annotation { "Feature Type Name" : "Feature", "Feature Type Description" : "" }
export const myFeature = defineFeature(function(context is Context, id is Id, definition is map)
    precondition{}
    {
        {
            var Q0;
            Q0=qCreatedBy(makeId("Front.planeOp"),FACE);
            var sketch = newSketch(context, id + "F0", { "sketchPlane" : qUnion([Q0])});
            skCircle(sketch, "E0", {"center": v(0, 0) * mm, "radius": 11 * mm});
            skCircle(sketch, "E1", {"center": v(0, 0) * mm, "radius": 14.29 * mm});
            skCircle(sketch, "E2", {"center": v(0, 31.75) * mm, "radius": 11 * mm});
            skCircle(sketch, "E3", {"center": v(0, 31.75) * mm, "radius": 14.29 * mm});
            skCircle(sketch, "E4.1.0", {"center": v(-27.5, -15.87) * mm, "radius": 14.29 * mm});
            skCircle(sketch, "E4.1.1", {"center": v(-27.5, -15.87) * mm, "radius": 11 * mm});
            skCircle(sketch, "E4.2.0", {"center": v(27.5, -15.88) * mm, "radius": 14.29 * mm});
            skCircle(sketch, "E4.2.1", {"center": v(27.5, -15.88) * mm, "radius": 11 * mm});
            skSolve(sketch);
        }
        {
            var Q0;
            Q0=qCreatedBy(makeId("Front.planeOp"),FACE);
            var sketch = newSketch(context, id + "F1", { "sketchPlane" : qUnion([Q0])});
            skCircle(sketch, "E5.0", {"center": v(0, 31.75) * mm, "radius": 11 * mm});
            skCircle(sketch, "E6.0", {"center": v(0, 31.75) * mm, "radius": 14.29 * mm});
            skCircle(sketch, "E7.0", {"center": v(0, 0) * mm, "radius": 14.29 * mm});
            skCircle(sketch, "E8.0", {"center": v(0, 0) * mm, "radius": 11 * mm});
            skCircle(sketch, "E9.0", {"center": v(-27.5, -15.87) * mm, "radius": 14.29 * mm});
            skCircle(sketch, "E10.0", {"center": v(-27.5, -15.87) * mm, "radius": 11 * mm});
            skCircle(sketch, "E11.0", {"center": v(27.5, -15.88) * mm, "radius": 14.29 * mm});
            skCircle(sketch, "E12.0", {"center": v(27.5, -15.88) * mm, "radius": 11 * mm});
            skCircle(sketch, "E13", {"center": v(0, 0) * mm, "radius": 31.75 * mm});
            skCircle(sketch, "E14", {"center": v(0, 0) * mm, "radius": 28.58 * mm});
            skPoint(sketch, "E15", {"position": v(-28.53, -1.62) * mm});
            skPoint(sketch, "E16", {"position": v(-12.86, 25.52) * mm});
            skArc(sketch, "E17", {"start": v(-28.53, -1.62) * mm, "mid": v(-19, 10.96) * mm, "end": v(-12.86, 25.52) * mm});
            skArc(sketch, "E18.1.0", {"start": v(15.67, -23.9) * mm, "mid": v(0, -21.93) * mm, "end": v(-15.67, -23.9) * mm});
            skArc(sketch, "E18.2.0", {"start": v(12.86, 25.52) * mm, "mid": v(19, 10.96) * mm, "end": v(28.53, -1.62) * mm});
            skPoint(sketch, "E19", {"position": v(12.86, 25.52) * mm});
            skPoint(sketch, "E20", {"position": v(28.53, -1.62) * mm});
            skPoint(sketch, "E21", {"position": v(15.67, -23.9) * mm});
            skPoint(sketch, "E22", {"position": v(-15.67, -23.9) * mm});
            skPoint(sketch, "E23", {"position": v(-39.01, -51.78) * mm});
            skSolve(sketch);
        }
        {
            var Q0;
            Q0=qCreatedBy(makeId("Front.planeOp"),FACE);
            var sketch = newSketch(context, id + "F2", { "sketchPlane" : qUnion([Q0])});
            skCircle(sketch, "E24.0.0", {"center": v(0, 31.75) * mm, "radius": 11 * mm});
            skArc(sketch, "E25.0", {"start": v(-12.86, 25.52) * mm, "mid": v(-8.37, 20.17) * mm, "end": v(-1.88, 17.59) * mm});
            skArc(sketch, "E26.0", {"start": v(-15.34, 27.8) * mm, "mid": v(-27.5, 15.87) * mm, "end": v(-31.74, -0.61) * mm});
            skArc(sketch, "E27.0", {"start": v(-16.71, 23.18) * mm, "mid": v(-24.75, 14.29) * mm, "end": v(-28.43, 2.89) * mm});
            skArc(sketch, "E28.0", {"start": v(-28.53, -1.62) * mm, "mid": v(-19, 10.96) * mm, "end": v(-12.86, 25.52) * mm});
            skArc(sketch, "E29.0", {"start": v(12.86, 25.52) * mm, "mid": v(19, 10.96) * mm, "end": v(28.53, -1.62) * mm});
            skArc(sketch, "E30.0", {"start": v(-1.88, 14.16) * mm, "mid": v(-12.39, 7.12) * mm, "end": v(-13.18, -5.51) * mm});
            skArc(sketch, "E31.0.0", {"start": v(15.67, -23.9) * mm, "mid": v(13.28, -17.3) * mm, "end": v(14.31, -10.36) * mm});
            skArc(sketch, "E31.0.1", {"start": v(28.53, -1.62) * mm, "mid": v(19, 10.96) * mm, "end": v(12.86, 25.52) * mm});
            skArc(sketch, "E31.0.2", {"start": v(12.86, 25.52) * mm, "mid": v(8.34, 20.15) * mm, "end": v(1.82, 17.58) * mm});
            skArc(sketch, "E31.0.3", {"start": v(-12.86, 25.52) * mm, "mid": v(-19, 10.96) * mm, "end": v(-28.53, -1.62) * mm});
            skArc(sketch, "E31.0.4", {"start": v(-28.53, -1.62) * mm, "mid": v(-21.62, -2.85) * mm, "end": v(-16.13, -7.21) * mm});
            skArc(sketch, "E31.0.5", {"start": v(-15.67, -23.9) * mm, "mid": v(0, -21.93) * mm, "end": v(15.67, -23.9) * mm});
            skArc(sketch, "E32.0", {"start": v(21.89, -29.02) * mm, "mid": v(39.87, -23.02) * mm, "end": v(36.07, -4.45) * mm});
            skArc(sketch, "E33.0.0", {"start": v(-11.71, -26.06) * mm, "mid": v(0, -28.58) * mm, "end": v(11.71, -26.06) * mm});
            skArc(sketch, "E33.0.1", {"start": v(15.67, -23.9) * mm, "mid": v(0, -21.93) * mm, "end": v(-15.67, -23.9) * mm});
            skArc(sketch, "E34.0", {"start": v(-16.13, -7.21) * mm, "mid": v(-21.62, -2.85) * mm, "end": v(-28.53, -1.62) * mm});
            skArc(sketch, "E35.0.0", {"start": v(-36.07, -4.45) * mm, "mid": v(-39.87, -23.02) * mm, "end": v(-21.89, -29.02) * mm});
            skCircle(sketch, "E36.0", {"center": v(-27.5, -15.87) * mm, "radius": 11 * mm});
            skCircle(sketch, "E37.0", {"center": v(27.5, -15.88) * mm, "radius": 11 * mm});
            skCircle(sketch, "E38.0.0", {"center": v(0, 0) * mm, "radius": 11 * mm});
            skArc(sketch, "E39", {"start": v(-36.67, -4.93) * mm, "mid": v(-34.15, -2.84) * mm, "end": v(-31.74, -0.61) * mm});
            skArc(sketch, "E40.1.0", {"start": v(22.6, -29.3) * mm, "mid": v(19.53, -28.16) * mm, "end": v(16.4, -27.18) * mm});
            skArc(sketch, "E40.2.0", {"start": v(14.07, 34.22) * mm, "mid": v(14.62, 31) * mm, "end": v(15.34, 27.8) * mm});
            skPoint(sketch, "E41", {"position": v(-28.43, 2.89) * mm});
            skPoint(sketch, "E42", {"position": v(-16.71, 23.18) * mm});
            skPoint(sketch, "E43", {"position": v(16.71, 23.18) * mm});
            skPoint(sketch, "E44", {"position": v(28.43, 2.89) * mm});
            skPoint(sketch, "E45", {"position": v(-11.71, -26.06) * mm});
            skPoint(sketch, "E46", {"position": v(11.71, -26.06) * mm});
            skArc(sketch, "E47.trimOffspring", {"start": v(-15.34, 27.8) * mm, "mid": v(-14.62, 31) * mm, "end": v(-14.07, 34.22) * mm});
            skArc(sketch, "E48.trimOffspring", {"start": v(-28.43, 2.89) * mm, "mid": v(-21.58, 12.46) * mm, "end": v(-16.71, 23.18) * mm});
            skArc(sketch, "E49.trimOffspring", {"start": v(16.71, 23.18) * mm, "mid": v(21.58, 12.46) * mm, "end": v(28.43, 2.89) * mm});
            skArc(sketch, "E50.trimOffspring", {"start": v(31.74, -0.61) * mm, "mid": v(34.15, -2.84) * mm, "end": v(36.67, -4.93) * mm});
            skArc(sketch, "E51.trimOffspring", {"start": v(28.43, 2.89) * mm, "mid": v(24.75, 14.29) * mm, "end": v(16.71, 23.18) * mm});
            skArc(sketch, "E52.trimOffspring", {"start": v(31.74, -0.61) * mm, "mid": v(27.5, 15.87) * mm, "end": v(15.34, 27.8) * mm});
            skArc(sketch, "E53.trimOffspring", {"start": v(11.71, -26.06) * mm, "mid": v(0, -24.92) * mm, "end": v(-11.71, -26.06) * mm});
            skArc(sketch, "E54.trimOffspring", {"start": v(-16.4, -27.18) * mm, "mid": v(-19.53, -28.16) * mm, "end": v(-22.6, -29.3) * mm});
            skArc(sketch, "E55.trimOffspring", {"start": v(-16.4, -27.18) * mm, "mid": v(0, -31.75) * mm, "end": v(16.4, -27.18) * mm});
            skArc(sketch, "E56.trimOffspring", {"start": v(-11.71, -26.06) * mm, "mid": v(0, -28.57) * mm, "end": v(11.71, -26.06) * mm});
            skArc(sketch, "E57.trimOffspring", {"start": v(-15.67, -23.9) * mm, "mid": v(-13.28, -17.33) * mm, "end": v(-14.3, -10.42) * mm});
            skArc(sketch, "E58.trimOffspring", {"start": v(14.18, 33.46) * mm, "mid": v(0, 46.04) * mm, "end": v(-14.18, 33.46) * mm});
            skLineSegment(sketch, "E59", {"start": v(-1.88, 17.59) * mm, "end": v(-1.88, 14.16) * mm});
            skLineSegment(sketch, "E60", {"start": v(1.82, 17.58) * mm, "end": v(1.82, 14.17) * mm});
            skLineSegment(sketch, "E61.1.0", {"start": v(-16.13, -7.21) * mm, "end": v(-13.18, -5.51) * mm});
            skLineSegment(sketch, "E61.1.1", {"start": v(-14.3, -10.42) * mm, "end": v(-11.33, -8.71) * mm});
            skLineSegment(sketch, "E61.2.0", {"start": v(14.31, -10.36) * mm, "end": v(11.36, -8.66) * mm});
            skLineSegment(sketch, "E61.2.1", {"start": v(16.17, -7.16) * mm, "end": v(13.2, -5.45) * mm});
            skArc(sketch, "E62.trimOffspring", {"start": v(-14.3, -10.42) * mm, "mid": v(-13.28, -17.33) * mm, "end": v(-15.67, -23.9) * mm});
            skArc(sketch, "E63.trimOffspring", {"start": v(16.17, -7.16) * mm, "mid": v(21.65, -2.84) * mm, "end": v(28.53, -1.62) * mm});
            skArc(sketch, "E64.trimOffspring", {"start": v(-1.88, 17.59) * mm, "mid": v(-8.37, 20.17) * mm, "end": v(-12.86, 25.52) * mm});
            skArc(sketch, "E65.trimOffspring", {"start": v(1.82, 17.58) * mm, "mid": v(8.34, 20.15) * mm, "end": v(12.86, 25.52) * mm});
            skArc(sketch, "E66.trimOffspring", {"start": v(-11.33, -8.71) * mm, "mid": v(0.03, -14.29) * mm, "end": v(11.36, -8.66) * mm});
            skArc(sketch, "E67.trimOffspring", {"start": v(13.2, -5.45) * mm, "mid": v(12.36, 7.17) * mm, "end": v(1.82, 14.17) * mm});
            skSolve(sketch);
        }
        {
            var Q0;
            Q0=makeQuery(id+"F2.imprint","IMPRINT",FACE,{"disambiguationData":[TD([[makeQuery(id+"F2.imprint","IMPRINT",EDGE,{"derivedFrom":sQuery(id+"F2.wireOp",EDGE,"E30.0")}),1.0]])]});
            var Q1;
            {var subQ4=sQuery(id+"F2.wireOp",EDGE,"E26.0");Q1=makeQuery(id+"F2.imprint","IMPRINT",FACE,{"disambiguationData":[TD([[makeQuery(id+"F2.imprint","IMPRINT",EDGE,{"derivedFrom":subQ4}),1.0]])]});}
            var Q2;
            {var subQ1=sQuery(id+"F2.wireOp",EDGE,"E33.0.1");Q2=makeQuery(id+"F2.imprint","IMPRINT",FACE,{"disambiguationData":[TD([[makeQuery(id+"F2.imprint","IMPRINT",EDGE,{"derivedFrom":subQ1}),1.0]])]});}
            var Q3;
            {var subQ4=sQuery(id+"F2.wireOp",EDGE,"E31.0.1");Q3=makeQuery(id+"F2.imprint","IMPRINT",FACE,{"disambiguationData":[TD([[makeQuery(id+"F2.imprint","IMPRINT",EDGE,{"derivedFrom":subQ4}),-1.0]])]});}
            var Q4;
            {var subQ0=sQuery(id+"F1.wireOp",EDGE,"E14");var subQ5=sQuery(id+"F1.wireOp",EDGE,"E10.0");var subQ6=makeQuery(id+"F1.imprint","INTERSECT",VERTEX,{"disambiguationData":[OD(1.0)],"derivedFrom":[subQ5,subQ0]});Q4=makeQuery(id+"F1.imprint","IMPRINT",FACE,{"disambiguationData":[TD([[makeQuery(id+"F1.imprint","IMPRINT",EDGE,{"disambiguationData":[TD([[subQ6,-1.0]])],"derivedFrom":subQ5}),-1.0]])]});}
            var Q5;
            {var subQ0=sQuery(id+"F2.wireOp",EDGE,"e14fca99-027b-4c28-9753-7c88e60515db.trimOffspring");var subQ5=sQuery(id+"F2.wireOp",EDGE,"E36.0");var subQ6=makeQuery(id+"F2.imprint","INTERSECT",VERTEX,{"disambiguationData":[OD(0.0)],"derivedFrom":[subQ5,subQ0]});Q5=makeQuery(id+"F2.imprint","IMPRINT",FACE,{"disambiguationData":[TD([[makeQuery(id+"F2.imprint","IMPRINT",EDGE,{"disambiguationData":[TD([[subQ6,1.0]])],"derivedFrom":subQ5}),-1.0]])]});}
            var Q6;
            Q6=makeQuery(id+"F0.imprint","IMPRINT",FACE,{"disambiguationData":[TD([[makeQuery(id+"F0.imprint","IMPRINT",EDGE,{"derivedFrom":sQuery(id+"F0.wireOp",EDGE,"E4.1.0")}),1.0]])]});
            var Q7;
            {var subQ0=sQuery(id+"F1.wireOp",EDGE,"E13");var subQ1=sQuery(id+"F1.wireOp",EDGE,"E11.0");var subQ2=makeQuery(id+"F1.imprint","INTERSECT",VERTEX,{"disambiguationData":[OD(0.0)],"derivedFrom":[subQ1,subQ0]});Q7=makeQuery(id+"F1.imprint","IMPRINT",FACE,{"disambiguationData":[TD([[makeQuery(id+"F1.imprint","IMPRINT",EDGE,{"disambiguationData":[TD([[subQ2,1.0]])],"derivedFrom":subQ1}),1.0]])]});}
            var Q8;
            {var subQ4=sQuery(id+"F2.wireOp",EDGE,"5d4614e1-1f50-464f-81f7-e68e0fa5c01f.trimOffspring");var subQ6=sQuery(id+"F2.wireOp",EDGE,"E24.0.0");var subQ12=makeQuery(id+"F2.imprint","INTERSECT",VERTEX,{"disambiguationData":[OD(0.0)],"derivedFrom":[subQ6,subQ4]});Q8=makeQuery(id+"F2.imprint","IMPRINT",FACE,{"disambiguationData":[TD([[makeQuery(id+"F2.imprint","IMPRINT",EDGE,{"disambiguationData":[TD([[subQ12,1.0]])],"derivedFrom":subQ6}),-1.0]])]});}
            extrude(context, id + "F3", {"entities" : qUnion([Q0, Q1, Q2, Q3, Q4, Q5, Q6, Q7, Q8]), "oppositeDirection" : true, "depth" : 6.35 * mm, "offsetDistance" : 25.4 * mm});
        }
        {
            var Q0;
            Q0=makeQuery(id+"F3.opExtrude","CAP_FACE",FACE,{"disambiguationData":[OSD([sQuery(id+"F2.wireOp",EDGE,"E24.0.0"),sQuery(id+"F2.wireOp",EDGE,"E26.0"),sQuery(id+"F2.wireOp",EDGE,"E27.0"),sQuery(id+"F2.wireOp",EDGE,"E30.0"),sQuery(id+"F2.wireOp",EDGE,"E31.0.0"),sQuery(id+"F2.wireOp",EDGE,"E31.0.1"),sQuery(id+"F2.wireOp",EDGE,"E31.0.3"),sQuery(id+"F2.wireOp",EDGE,"E32.0"),sQuery(id+"F2.wireOp",EDGE,"E33.0.1"),sQuery(id+"F2.wireOp",EDGE,"E36.0"),sQuery(id+"F2.wireOp",EDGE,"E37.0"),sQuery(id+"F2.wireOp",EDGE,"E38.0.0"),sQuery(id+"F2.wireOp",EDGE,"E39"),sQuery(id+"F2.wireOp",EDGE,"E40.1.0"),sQuery(id+"F2.wireOp",EDGE,"E40.2.0"),sQuery(id+"F2.wireOp",EDGE,"E47.trimOffspring"),sQuery(id+"F2.wireOp",EDGE,"E48.trimOffspring"),sQuery(id+"F2.wireOp",EDGE,"E49.trimOffspring"),sQuery(id+"F2.wireOp",EDGE,"E50.trimOffspring"),sQuery(id+"F2.wireOp",EDGE,"E51.trimOffspring"),sQuery(id+"F2.wireOp",EDGE,"E52.trimOffspring"),sQuery(id+"F2.wireOp",EDGE,"E53.trimOffspring"),sQuery(id+"F2.wireOp",EDGE,"E54.trimOffspring"),sQuery(id+"F2.wireOp",EDGE,"E55.trimOffspring"),sQuery(id+"F2.wireOp",EDGE,"E56.trimOffspring"),sQuery(id+"F2.wireOp",EDGE,"E58.trimOffspring"),sQuery(id+"F2.wireOp",EDGE,"E59"),sQuery(id+"F2.wireOp",EDGE,"E60"),sQuery(id+"F2.wireOp",EDGE,"E61.1.0"),sQuery(id+"F2.wireOp",EDGE,"E61.1.1"),sQuery(id+"F2.wireOp",EDGE,"E61.2.0"),sQuery(id+"F2.wireOp",EDGE,"E61.2.1"),sQuery(id+"F2.wireOp",EDGE,"E34.0"),sQuery(id+"F2.wireOp",EDGE,"E63.trimOffspring"),sQuery(id+"F2.wireOp",EDGE,"E64.trimOffspring"),sQuery(id+"F2.wireOp",EDGE,"E65.trimOffspring"),sQuery(id+"F2.wireOp",EDGE,"E66.trimOffspring"),sQuery(id+"F2.wireOp",EDGE,"E67.trimOffspring"),sQuery(id+"F2.wireOp",EDGE,"E57.trimOffspring"),sQuery(id+"F2.wireOp",EDGE,"E35.0.0")])],"isStart":true});
            var sketch = newSketch(context, id + "F4", { "sketchPlane" : qUnion([Q0])});
            skText(sketch, "E68", { "text": "Aditi Arun", "fontName": "OpenSans-BoldItalic.ttf"});
            const initialGuessF4  = {"E68": [-0.00517, 0.01133, 1, 0, 0.00155]};
            skSetInitialGuess(sketch, initialGuessF4);
            skSolve(sketch);
        }
        {
            var Q0;
            Q0 = qSketchRegion(id + "F4", true);
            extrude(context, id + "F5", {"entities" : qUnion([Q0]), "operationType" : NewBodyOperationType.REMOVE, "oppositeDirection" : true, "depth" : 3.17 * mm, "offsetDistance" : 25.4 * mm});
        }
    });